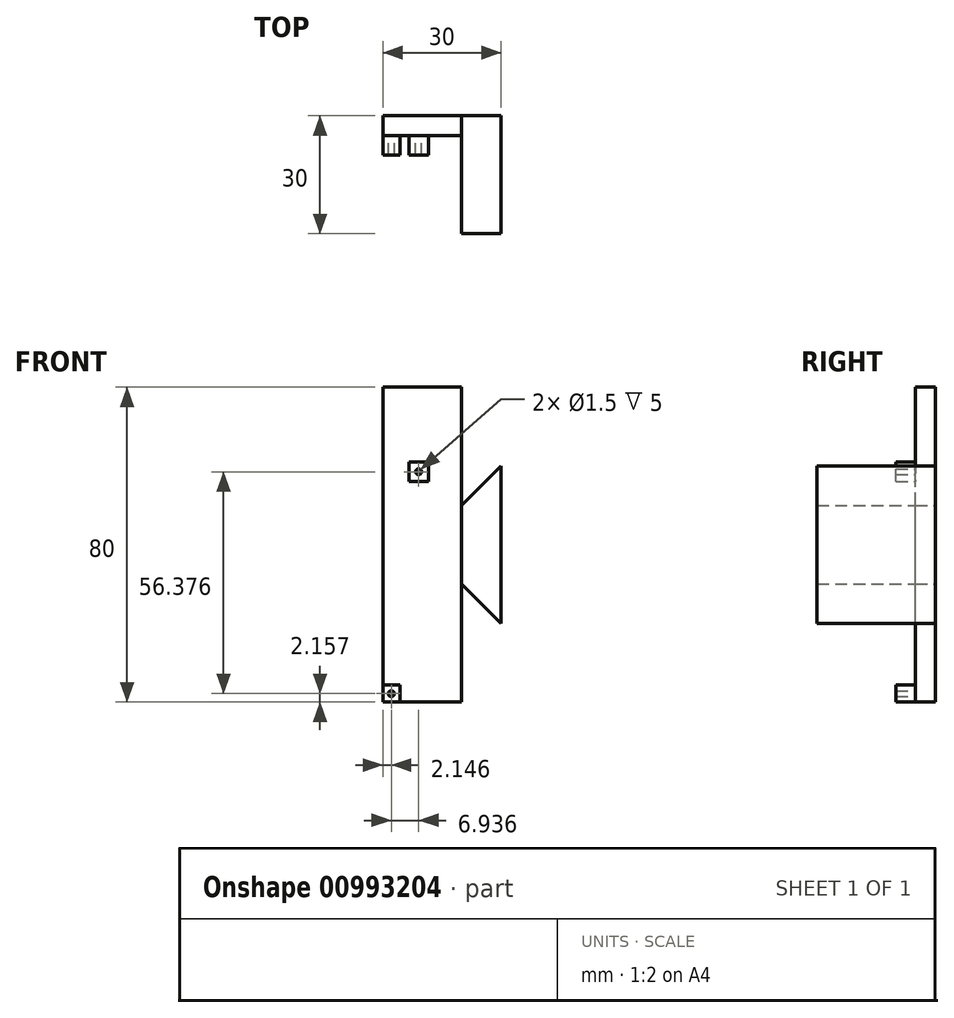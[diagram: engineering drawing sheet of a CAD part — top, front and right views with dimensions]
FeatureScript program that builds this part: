
annotation { "Feature Type Name" : "Feature", "Feature Type Description" : "" }
export const myFeature = defineFeature(function(context is Context, id is Id, definition is map)
    precondition{}
    {
        {
            var Q0;
            Q0=qCreatedBy(makeId("Front.planeOp"),FACE);
            var sketch = newSketch(context, id + "F0", { "sketchPlane" : qUnion([Q0])});
            skLineSegment(sketch, "E0.bottom", {"start": v(10, -40) * mm, "end": v(-10, -40) * mm});
            skLineSegment(sketch, "E0.top", {"start": v(10, 40) * mm, "end": v(-10, 40) * mm});
            skLineSegment(sketch, "E0.left", {"start": v(10, -40) * mm, "end": v(10, 40) * mm});
            skLineSegment(sketch, "E0.right", {"start": v(-10, -40) * mm, "end": v(-10, 40) * mm});
            skPoint(sketch, "E0.middle", {"position": v(0, 0) * mm});
            skSolve(sketch);
        }
        {
            var Q0;
            Q0 = qSketchRegion(id + "F0", true);
            extrude(context, id + "F1", {"entities" : qUnion([Q0]), "depth" : 5 * mm, "offsetDistance" : 25 * mm});
        }
        {
            var Q0;
            {var subQ0=sQuery(id+"F0.wireOp",EDGE,"E0.left");var subQ1=sQuery(id+"F0.wireOp",EDGE,"E0.top");var subQ2=sQuery(id+"F0.wireOp",EDGE,"E0.right");var subQ3=sQuery(id+"F0.wireOp",EDGE,"E0.bottom");Q0=makeQuery(id+"F4.boolean.opBoolean","SPLIT",FACE,{"disambiguationData":[TD([makeQuery(id+"F1.opExtrude","SWEPT_FACE",FACE,{"disambiguationData":[OSD([subQ3])]})])],"derivedFrom":makeQuery(id+"F1.opExtrude","CAP_FACE",FACE,{"disambiguationData":[OSD([subQ3,subQ1,subQ0,subQ2])],"isStart":false})});}
            var sketch = newSketch(context, id + "F2", { "sketchPlane" : qUnion([Q0])});
            skCircle(sketch, "E1", {"center": v(-7.85, -37.84) * mm, "radius": 0.75 * mm});
            skLineSegment(sketch, "E2.bottom", {"start": v(-10, -35.69) * mm, "end": v(-5.7, -35.69) * mm});
            skLineSegment(sketch, "E2.top", {"start": v(-10, -40) * mm, "end": v(-5.7, -40) * mm});
            skLineSegment(sketch, "E2.left", {"start": v(-10, -35.69) * mm, "end": v(-10, -40) * mm});
            skLineSegment(sketch, "E2.right", {"start": v(-5.7, -35.69) * mm, "end": v(-5.7, -40) * mm});
            skSolve(sketch);
        }
        {
            var Q0;
            Q0=qCreatedBy(makeId("Front.planeOp"),FACE);
            var sketch = newSketch(context, id + "F3", { "sketchPlane" : qUnion([Q0])});
            skCircle(sketch, "E3", {"center": v(-0.92, 18.53) * mm, "radius": 0.75 * mm});
            skLineSegment(sketch, "E4.bottom", {"start": v(1.58, 16.03) * mm, "end": v(-3.42, 16.03) * mm});
            skLineSegment(sketch, "E4.top", {"start": v(1.58, 21.03) * mm, "end": v(-3.42, 21.03) * mm});
            skLineSegment(sketch, "E4.left", {"start": v(1.58, 16.03) * mm, "end": v(1.58, 21.03) * mm});
            skLineSegment(sketch, "E4.right", {"start": v(-3.42, 16.03) * mm, "end": v(-3.42, 21.03) * mm});
            skSolve(sketch);
        }
        {
            var Q0;
            Q0 = qSketchRegion(id + "F3", true);
            extrude(context, id + "F4", {"entities" : qUnion([Q0]), "operationType" : NewBodyOperationType.ADD, "depth" : 10 * mm, "offsetDistance" : 25 * mm});
        }
        {
            var Q0;
            Q0 = qSketchRegion(id + "F2", true);
            extrude(context, id + "F5", {"entities" : qUnion([Q0]), "operationType" : NewBodyOperationType.ADD, "depth" : 5 * mm, "offsetDistance" : 25 * mm});
        }
        {
            var Q0;
            Q0=qCreatedBy(makeId("Front.planeOp"),FACE);
            var sketch = newSketch(context, id + "F6", { "sketchPlane" : qUnion([Q0])});
            skLineSegment(sketch, "E5.bottom", {"start": v(10, -10) * mm, "end": v(20, -10) * mm});
            skLineSegment(sketch, "E5.top", {"start": v(10, 10) * mm, "end": v(20, 10) * mm});
            skLineSegment(sketch, "E5.left", {"start": v(10, -10) * mm, "end": v(10, 10) * mm});
            skLineSegment(sketch, "E5.right", {"start": v(20, -10) * mm, "end": v(20, 10) * mm});
            skLineSegment(sketch, "E6", {"start": v(10, -10) * mm, "end": v(20, -20) * mm});
            skLineSegment(sketch, "E7", {"start": v(20, -20) * mm, "end": v(20, -10) * mm});
            skLineSegment(sketch, "E8", {"start": v(10, 10) * mm, "end": v(20, 20) * mm});
            skLineSegment(sketch, "E9", {"start": v(20, 20) * mm, "end": v(20, 10) * mm});
            skSolve(sketch);
        }
        {
            var Q0;
            Q0 = qSketchRegion(id + "F6", true);
            extrude(context, id + "F7", {"entities" : qUnion([Q0]), "operationType" : NewBodyOperationType.ADD, "depth" : 30 * mm, "offsetDistance" : 25 * mm});
        }
    });
